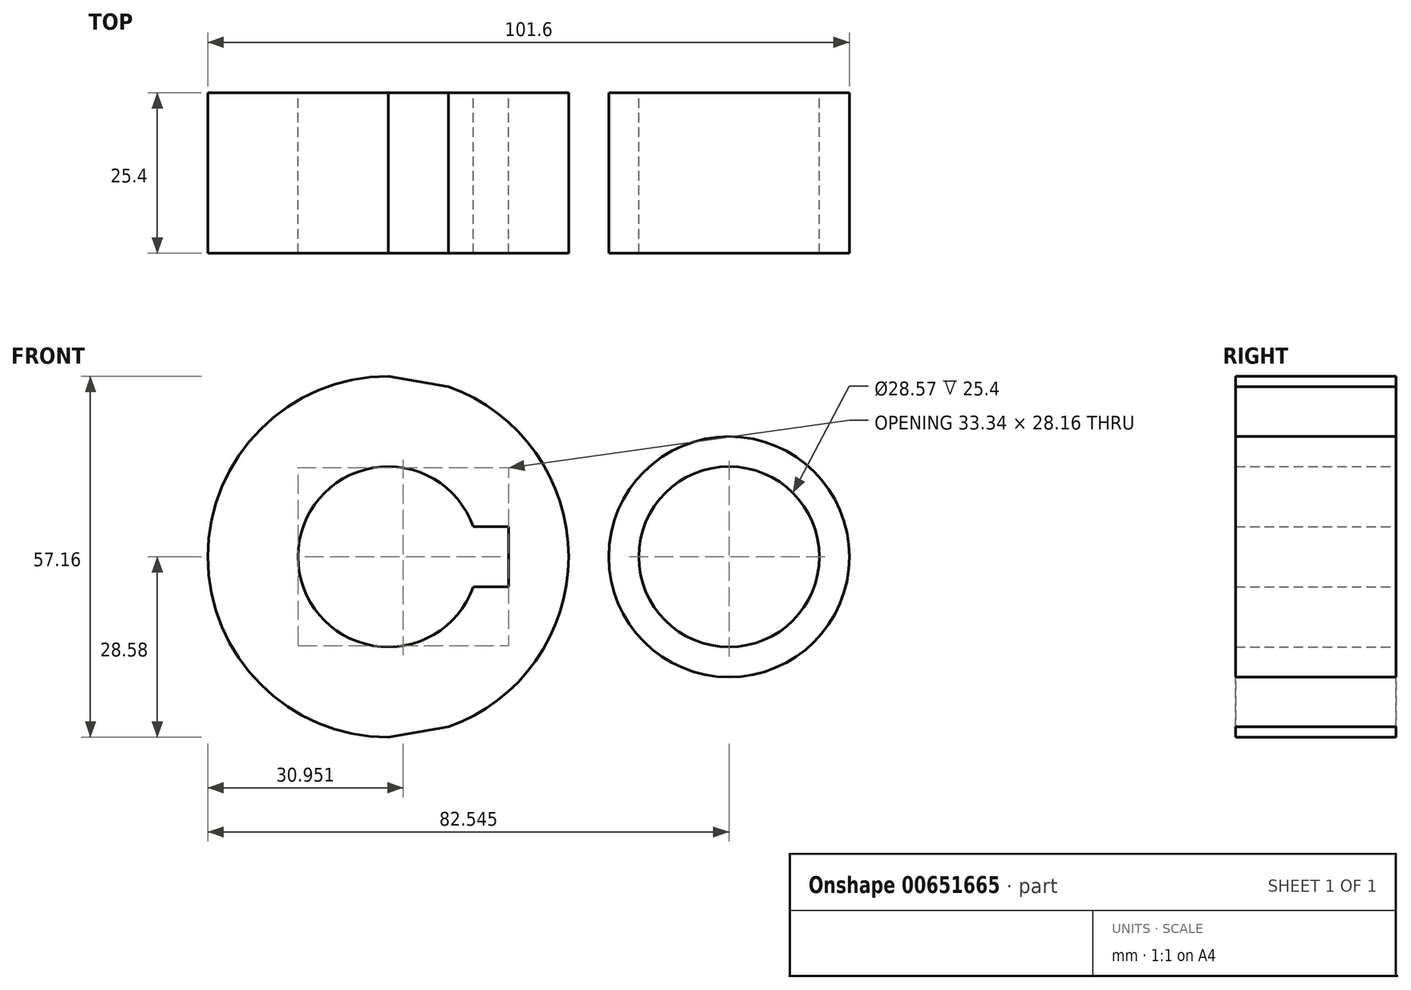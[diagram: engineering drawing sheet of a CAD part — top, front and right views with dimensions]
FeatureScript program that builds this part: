
annotation { "Feature Type Name" : "Feature", "Feature Type Description" : "" }
export const myFeature = defineFeature(function(context is Context, id is Id, definition is map)
    precondition{}
    {
        {
            var Q0;
            Q0=qCreatedBy(makeId("Front.planeOp"),FACE);
            var sketch = newSketch(context, id + "F0", { "sketchPlane" : qUnion([Q0])});
            skCircle(sketch, "E0", {"center": v(0, 0) * mm, "radius": 28.58 * mm});
            skCircle(sketch, "E1", {"center": v(53.98, 0) * mm, "radius": 19.05 * mm});
            skLineSegment(sketch, "E2", {"start": v(0, 28.57) * mm, "end": v(57.2, 18.78) * mm});
            skLineSegment(sketch, "E3", {"start": v(0, -28.58) * mm, "end": v(57.2, -18.78) * mm});
            skCircle(sketch, "E4", {"center": v(0, 0) * mm, "radius": 14.29 * mm});
            skCircle(sketch, "E5", {"center": v(53.98, 0) * mm, "radius": 14.29 * mm});
            skLineSegment(sketch, "E6.bottom", {"start": v(-19.05, 4.76) * mm, "end": v(19.05, 4.76) * mm});
            skLineSegment(sketch, "E6.top", {"start": v(-19.05, -4.76) * mm, "end": v(19.05, -4.76) * mm});
            skLineSegment(sketch, "E6.left", {"start": v(-19.05, 4.76) * mm, "end": v(-19.05, -4.76) * mm});
            skLineSegment(sketch, "E6.right", {"start": v(19.05, 4.76) * mm, "end": v(19.05, -4.76) * mm});
            skSolve(sketch);
        }
        {
            var Q0;
            {var subQ4=sQuery(id+"F0.wireOp",EDGE,"E6.left");Q0=makeQuery(id+"F0.imprint","IMPRINT",FACE,{"disambiguationData":[TD([[makeQuery(id+"F0.imprint","IMPRINT",EDGE,{"derivedFrom":subQ4}),-1.0]])]});}
            var Q1;
            {var subQ5=sQuery(id+"F0.wireOp",EDGE,"E6.left");Q1=makeQuery(id+"F0.imprint","IMPRINT",FACE,{"disambiguationData":[TD([[makeQuery(id+"F0.imprint","IMPRINT",EDGE,{"derivedFrom":subQ5}),1.0]])]});}
            var Q2;
            {var subQ0=sQuery(id+"F0.wireOp",EDGE,"E2");var subQ1=sQuery(id+"F0.wireOp",EDGE,"E0");var subQ2=makeQuery(id+"F0.imprint","INTERSECT",VERTEX,{"disambiguationData":[OD(1.0)],"derivedFrom":[subQ1,subQ0]});Q2=makeQuery(id+"F0.imprint","IMPRINT",FACE,{"disambiguationData":[TD([[makeQuery(id+"F0.imprint","IMPRINT",EDGE,{"disambiguationData":[TD([[subQ2,1.0]])],"derivedFrom":subQ1}),-1.0]])]});}
            var Q3;
            Q3=makeQuery(id+"F0.imprint","IMPRINT",FACE,{"disambiguationData":[TD([[makeQuery(id+"F0.imprint","IMPRINT",EDGE,{"derivedFrom":sQuery(id+"F0.wireOp",EDGE,"E5")}),-1.0]])]});
            extrude(context, id + "F1", {"entities" : qUnion([Q0, Q1, Q2, Q3]), "depth" : 25.4 * mm, "offsetDistance" : 25.4 * mm});
        }
    });
